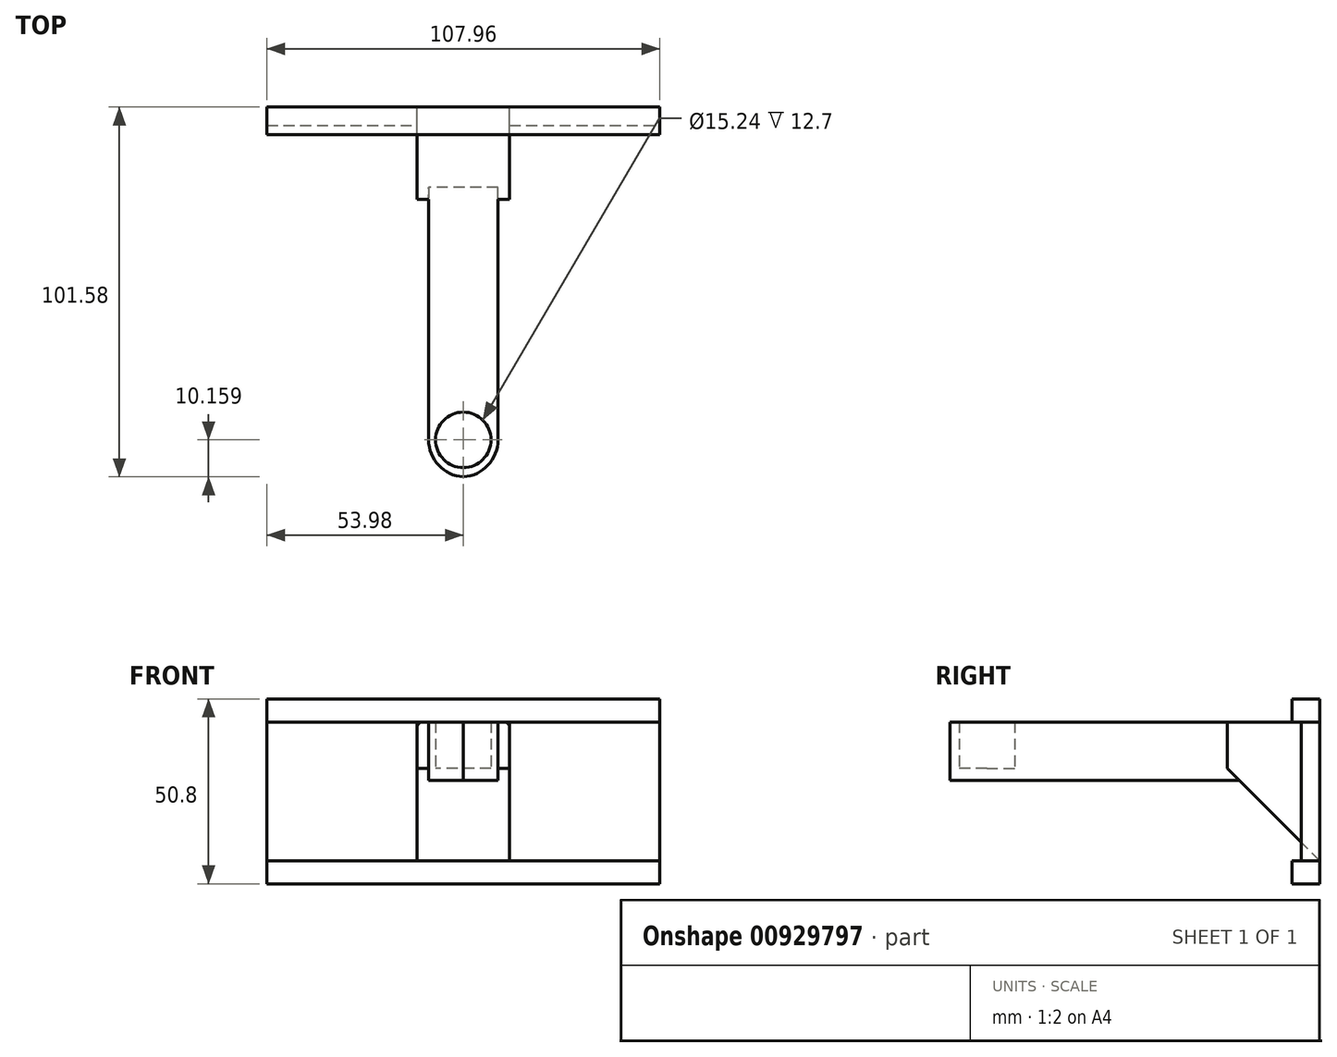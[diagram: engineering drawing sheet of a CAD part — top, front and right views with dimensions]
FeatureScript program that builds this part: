
annotation { "Feature Type Name" : "Feature", "Feature Type Description" : "" }
export const myFeature = defineFeature(function(context is Context, id is Id, definition is map)
    precondition{}
    {
        {
            var Q0;
            Q0=qCreatedBy(makeId("Front.planeOp"),FACE);
            var sketch = newSketch(context, id + "F0", { "sketchPlane" : qUnion([Q0])});
            skLineSegment(sketch, "E0.bottom", {"start": v(53.97, 25.4) * mm, "end": v(-53.98, 25.4) * mm});
            skLineSegment(sketch, "E0.top", {"start": v(53.98, -25.4) * mm, "end": v(-53.97, -25.4) * mm});
            skLineSegment(sketch, "E0.left", {"start": v(53.97, 25.4) * mm, "end": v(53.98, -25.4) * mm});
            skLineSegment(sketch, "E0.right", {"start": v(-53.98, 25.4) * mm, "end": v(-53.97, -25.4) * mm});
            skPoint(sketch, "E0.middle", {"position": v(0, 0) * mm});
            skLineSegment(sketch, "E1.bottom", {"start": v(12.7, 19.05) * mm, "end": v(-12.7, 19.05) * mm});
            skLineSegment(sketch, "E1.top", {"start": v(12.7, -19.05) * mm, "end": v(-12.7, -19.05) * mm});
            skLineSegment(sketch, "E1.left", {"start": v(12.7, 19.05) * mm, "end": v(12.7, -19.05) * mm});
            skLineSegment(sketch, "E1.right", {"start": v(-12.7, 19.05) * mm, "end": v(-12.7, -19.05) * mm});
            skPoint(sketch, "E2.middle", {"position": v(0, 11.84) * mm});
            skLineSegment(sketch, "E3.bottom", {"start": v(7.62, 18.19) * mm, "end": v(-7.62, 18.19) * mm});
            skLineSegment(sketch, "E3.top", {"start": v(7.62, 5.49) * mm, "end": v(-7.62, 5.49) * mm});
            skLineSegment(sketch, "E3.left", {"start": v(7.62, 18.19) * mm, "end": v(7.62, 5.49) * mm});
            skLineSegment(sketch, "E3.right", {"start": v(-7.62, 18.19) * mm, "end": v(-7.62, 5.49) * mm});
            skLineSegment(sketch, "E4.bottom", {"start": v(9.52, 19.05) * mm, "end": v(-9.52, 19.05) * mm});
            skLineSegment(sketch, "E4.top", {"start": v(9.52, 2.95) * mm, "end": v(-9.52, 2.95) * mm});
            skLineSegment(sketch, "E4.left", {"start": v(9.52, 19.05) * mm, "end": v(9.52, 2.95) * mm});
            skLineSegment(sketch, "E4.right", {"start": v(-9.52, 19.05) * mm, "end": v(-9.52, 2.95) * mm});
            skPoint(sketch, "E4.middle", {"position": v(0, 11) * mm});
            skPoint(sketch, "E4.middle.positionSnap0", {"position": v(0, 5.49) * mm});
            skPoint(sketch, "E4.centerSnap0", {"position": v(0, 5.49) * mm});
            skLineSegment(sketch, "E5", {"start": v(-7.62, 18.19) * mm, "end": v(-7.62, 19.05) * mm});
            skLineSegment(sketch, "E6", {"start": v(7.62, 18.19) * mm, "end": v(7.62, 19.05) * mm});
            skLineSegment(sketch, "E7.bottom", {"start": v(-53.98, 19.05) * mm, "end": v(53.98, 19.05) * mm});
            skLineSegment(sketch, "E7.top", {"start": v(-53.98, -19.05) * mm, "end": v(53.98, -19.05) * mm});
            skLineSegment(sketch, "E7.left", {"start": v(-53.98, 19.05) * mm, "end": v(-53.98, -19.05) * mm});
            skLineSegment(sketch, "E7.right", {"start": v(53.98, 19.05) * mm, "end": v(53.98, -19.05) * mm});
            skLineSegment(sketch, "E8.bottom", {"start": v(-53.98, 24.38) * mm, "end": v(53.98, 24.38) * mm});
            skLineSegment(sketch, "E8.top", {"start": v(-53.98, 20.07) * mm, "end": v(53.98, 20.07) * mm});
            skLineSegment(sketch, "E8.left", {"start": v(-53.98, 24.38) * mm, "end": v(-53.98, 20.07) * mm});
            skLineSegment(sketch, "E8.right", {"start": v(53.97, 24.38) * mm, "end": v(53.97, 20.07) * mm});
            skLineSegment(sketch, "E9.bottom", {"start": v(-53.98, -20.07) * mm, "end": v(53.97, -20.07) * mm});
            skLineSegment(sketch, "E9.top", {"start": v(-53.97, -24.38) * mm, "end": v(53.98, -24.38) * mm});
            skLineSegment(sketch, "E9.left", {"start": v(-53.97, -20.07) * mm, "end": v(-53.97, -24.38) * mm});
            skLineSegment(sketch, "E9.right", {"start": v(53.98, -20.07) * mm, "end": v(53.98, -24.38) * mm});
            skSolve(sketch);
        }
        {
            var Q0;
            Q0=makeQuery(id+"F0.imprint","IMPRINT",FACE,{"disambiguationData":[TD([[makeQuery(id+"F0.imprint","IMPRINT",EDGE,{"derivedFrom":sQuery(id+"F0.wireOp",EDGE,"E3.top")}),1.0]])]});
            var Q1;
            Q1=makeQuery(id+"F0.imprint","IMPRINT",FACE,{"disambiguationData":[TD([[makeQuery(id+"F0.imprint","IMPRINT",EDGE,{"derivedFrom":sQuery(id+"F0.wireOp",EDGE,"E3.bottom")}),1.0]])]});
            var Q2;
            Q2=makeQuery(id+"F0.imprint","IMPRINT",FACE,{"disambiguationData":[TD([[makeQuery(id+"F0.imprint","IMPRINT",EDGE,{"derivedFrom":sQuery(id+"F0.wireOp",EDGE,"E3.bottom")}),-1.0]])]});
            extrude(context, id + "F1", {"entities" : qUnion([Q0, Q1, Q2]), "depth" : 101.6 * mm, "offsetDistance" : 25.4 * mm});
        }
        {
            var Q0;
            Q0=makeQuery(id+"F0.imprint","IMPRINT",FACE,{"disambiguationData":[TD([[makeQuery(id+"F0.imprint","IMPRINT",EDGE,{"derivedFrom":sQuery(id+"F0.wireOp",EDGE,"E1.top")}),-1.0]])]});
            var Q1;
            Q1=makeQuery(id+"F0.imprint","IMPRINT",FACE,{"disambiguationData":[TD([[makeQuery(id+"F0.imprint","IMPRINT",EDGE,{"derivedFrom":sQuery(id+"F0.wireOp",EDGE,"E1.top")}),-1.0]])]});
            extrude(context, id + "F2", {"entities" : qUnion([Q0, Q1]), "operationType" : NewBodyOperationType.ADD, "depth" : 25.4 * mm, "offsetDistance" : 25.4 * mm});
        }
        {
            var Q0;
            Q0=qCreatedBy(makeId("Top.planeOp"),FACE);
            var sketch = newSketch(context, id + "F3", { "sketchPlane" : qUnion([Q0])});
            skCircle(sketch, "E10", {"center": v(0, -91.42) * mm, "radius": 7.62 * mm});
            skSolve(sketch);
        }
        {
            var Q0;
            Q0=makeQuery(id+"F3.imprint","IMPRINT",FACE,{"disambiguationData":[TD([[makeQuery(id+"F3.imprint","IMPRINT",EDGE,{"derivedFrom":sQuery(id+"F3.wireOp",EDGE,"E10")}),1.0]])]});
            extrude(context, id + "F4", {"entities" : qUnion([Q0]), "operationType" : NewBodyOperationType.REMOVE, "depth" : 25.15 * mm, "offsetDistance" : 25.4 * mm, "hasSecondDirection" : true, "secondDirectionOppositeDirection" : true, "secondDirectionDepth" : -6.35 * mm});
        }
        {
            var Q0;
            Q0=makeQuery(id+"F1.opExtrude","CAP_EDGE",EDGE,{"disambiguationData":[OSD([sQuery(id+"F0.wireOp",EDGE,"E4.left")])],"isStart":false});
            var Q1;
            Q1=makeQuery(id+"F1.opExtrude","CAP_EDGE",EDGE,{"disambiguationData":[OSD([sQuery(id+"F0.wireOp",EDGE,"E4.right")])],"isStart":false});
            fillet(context, id + "F5", {"entities" : qUnion([Q0, Q1]), "radius" : 10.16 * mm, "tangentPropagation" : true, "allowEdgeOverflow" : false});
        }
        {
            var Q0;
            {var subQ5=sQuery(id+"F0.wireOp",EDGE,"E1.right");Q0=makeQuery(id+"F0.imprint","IMPRINT",FACE,{"disambiguationData":[TD([[makeQuery(id+"F0.imprint","IMPRINT",EDGE,{"derivedFrom":subQ5}),-1.0]])]});}
            var Q1;
            {var subQ5=sQuery(id+"F0.wireOp",EDGE,"E1.left");Q1=makeQuery(id+"F0.imprint","IMPRINT",FACE,{"disambiguationData":[TD([[makeQuery(id+"F0.imprint","IMPRINT",EDGE,{"derivedFrom":subQ5}),1.0]])]});}
            extrude(context, id + "F6", {"entities" : qUnion([Q0, Q1]), "depth" : 5.08 * mm, "offsetDistance" : 25.4 * mm});
        }
        {
            var Q0;
            {var subQ1=sQuery(id+"F0.wireOp",EDGE,"E1.top");Q0=makeQuery(id+"F0.imprint","IMPRINT",FACE,{"disambiguationData":[TD([[makeQuery(id+"F0.imprint","IMPRINT",EDGE,{"derivedFrom":subQ1}),1.0]])]});}
            var Q1;
            {var subQ0=sQuery(id+"F0.wireOp",EDGE,"E0.top");Q1=makeQuery(id+"F0.imprint","IMPRINT",FACE,{"disambiguationData":[TD([[makeQuery(id+"F0.imprint","IMPRINT",EDGE,{"derivedFrom":subQ0}),-1.0]])]});}
            var Q2;
            {var subQ0=sQuery(id+"F0.wireOp",EDGE,"E9.bottom");Q2=makeQuery(id+"F0.imprint","IMPRINT",FACE,{"disambiguationData":[TD([[makeQuery(id+"F0.imprint","IMPRINT",EDGE,{"derivedFrom":subQ0}),-1.0]])]});}
            var Q3;
            {var subQ0=sQuery(id+"F0.wireOp",EDGE,"E8.bottom");Q3=makeQuery(id+"F0.imprint","IMPRINT",FACE,{"disambiguationData":[TD([[makeQuery(id+"F0.imprint","IMPRINT",EDGE,{"derivedFrom":subQ0}),-1.0]])]});}
            var Q4;
            {var subQ0=sQuery(id+"F0.wireOp",EDGE,"E0.bottom");Q4=makeQuery(id+"F0.imprint","IMPRINT",FACE,{"disambiguationData":[TD([[makeQuery(id+"F0.imprint","IMPRINT",EDGE,{"derivedFrom":subQ0}),1.0]])]});}
            var Q5;
            {var subQ6=sQuery(id+"F0.wireOp",EDGE,"E8.top");Q5=makeQuery(id+"F0.imprint","IMPRINT",FACE,{"disambiguationData":[TD([[makeQuery(id+"F0.imprint","IMPRINT",EDGE,{"derivedFrom":subQ6}),-1.0]])]});}
            extrude(context, id + "F7", {"entities" : qUnion([Q0, Q1, Q2, Q3, Q4, Q5]), "depth" : 7.62 * mm, "offsetDistance" : 25.4 * mm});
        }
        {
            var Q0;
            Q0=makeQuery(id+"F2.opExtrude","SWEPT_EDGE",EDGE,{"disambiguationData":[OSD([sQuery(id+"F0.wireOp",EDGE,"E1.bottom"),sQuery(id+"F0.wireOp",EDGE,"E1.right"),sQuery(id+"F0.wireOp",EDGE,"E7.bottom")])]});
            var Q1;
            Q1=makeQuery(id+"F2.opExtrude","SWEPT_EDGE",EDGE,{"disambiguationData":[OSD([sQuery(id+"F0.wireOp",EDGE,"E1.bottom"),sQuery(id+"F0.wireOp",EDGE,"E1.left"),sQuery(id+"F0.wireOp",EDGE,"E7.bottom")])]});
            fillet(context, id + "F8", {"entities" : qUnion([Q0, Q1]), "radius" : 1.52 * mm, "tangentPropagation" : true, "allowEdgeOverflow" : false});
        }
        {
            var Q0;
            Q0=makeQuery(id+"F2.opExtrude","CAP_EDGE",EDGE,{"disambiguationData":[OSD([sQuery(id+"F0.wireOp",EDGE,"E1.top")])],"isStart":false});
            chamfer(context, id + "F9", {"entities" : qUnion([Q0]), "width" : 25.4 * mm, "tangentPropagation" : true});
        }
    });
